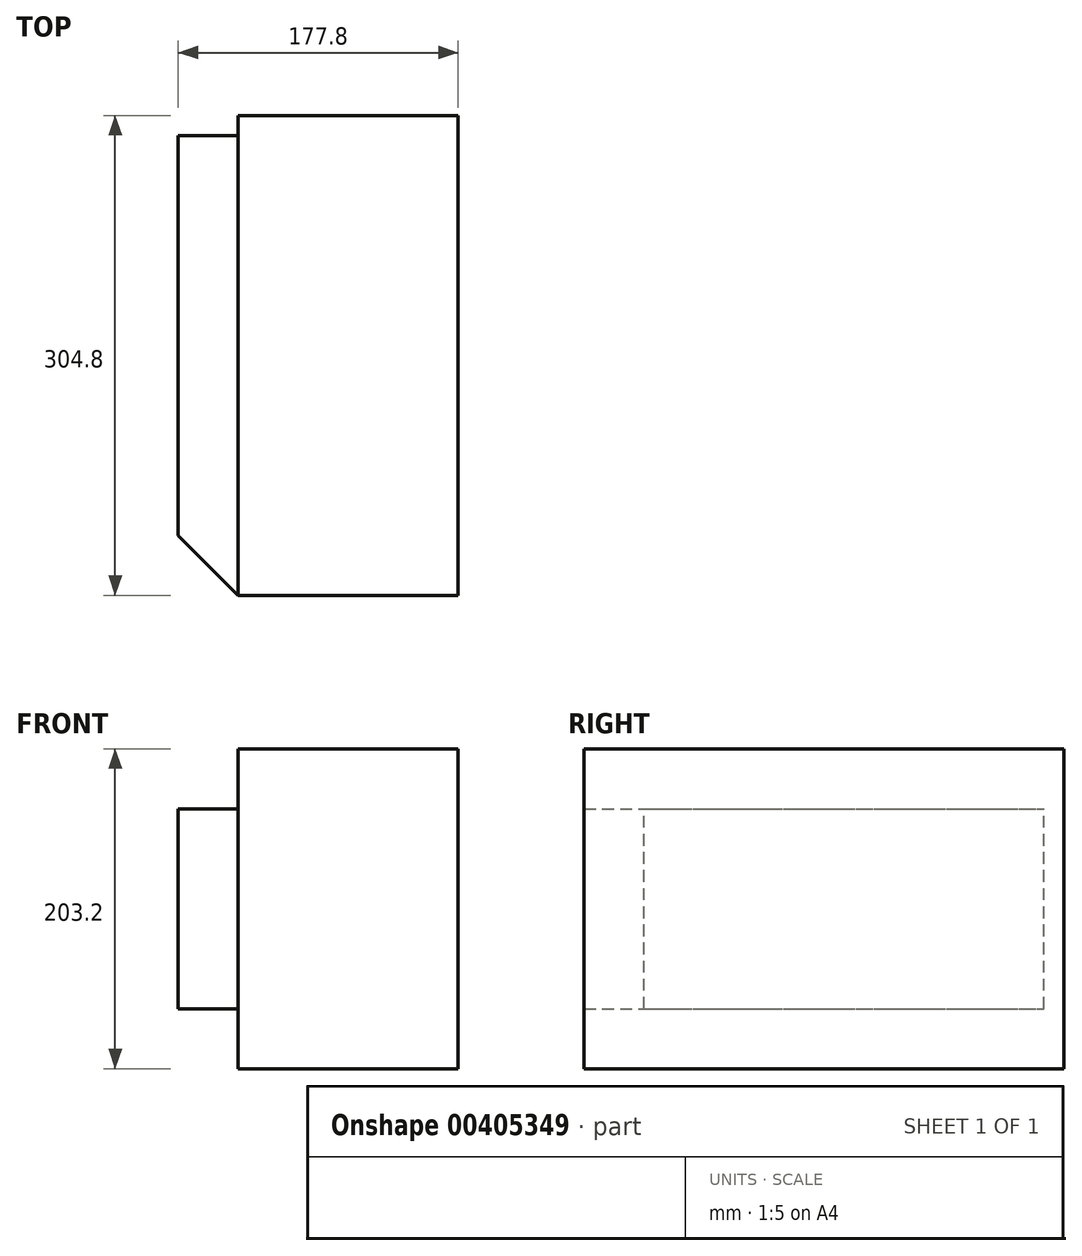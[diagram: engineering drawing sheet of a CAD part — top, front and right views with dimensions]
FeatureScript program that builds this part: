
annotation { "Feature Type Name" : "Feature", "Feature Type Description" : "" }
export const myFeature = defineFeature(function(context is Context, id is Id, definition is map)
    precondition{}
    {
        {
            var Q0;
            Q0=qCreatedBy(makeId("Front.planeOp"),FACE);
            var sketch = newSketch(context, id + "F0", { "sketchPlane" : qUnion([Q0])});
            skLineSegment(sketch, "E0.bottom", {"start": v(-126.61, 97) * mm, "end": v(51.19, 97) * mm});
            skLineSegment(sketch, "E0.top", {"start": v(-126.61, -106.2) * mm, "end": v(51.19, -106.2) * mm});
            skLineSegment(sketch, "E0.left", {"start": v(-126.61, 97) * mm, "end": v(-126.61, -106.2) * mm});
            skLineSegment(sketch, "E0.right", {"start": v(51.19, 97) * mm, "end": v(51.19, -106.2) * mm});
            skLineSegment(sketch, "E1.0", {"start": v(-88.51, 97) * mm, "end": v(-88.51, -106.2) * mm});
            skLineSegment(sketch, "E2", {"start": v(-126.61, 58.9) * mm, "end": v(-88.51, 58.9) * mm});
            skLineSegment(sketch, "E3", {"start": v(-126.61, -68.1) * mm, "end": v(-88.51, -68.1) * mm});
            skSolve(sketch);
        }
        {
            var Q0;
            {var subQ0=sQuery(id+"F0.wireOp",EDGE,"E0.right");Q0=makeQuery(id+"F0.imprint","IMPRINT",FACE,{"disambiguationData":[TD([[makeQuery(id+"F0.imprint","IMPRINT",EDGE,{"derivedFrom":subQ0}),-1.0]])]});}
            extrude(context, id + "F1", {"entities" : qUnion([Q0]), "depth" : 304.8 * mm});
        }
        {
            var Q0;
            {var subQ0=sQuery(id+"F0.wireOp",EDGE,"E2");Q0=makeQuery(id+"F0.imprint","IMPRINT",FACE,{"disambiguationData":[TD([[makeQuery(id+"F0.imprint","IMPRINT",EDGE,{"derivedFrom":subQ0}),-1.0]])]});}
            extrude(context, id + "F2", {"entities" : qUnion([Q0]), "operationType" : NewBodyOperationType.ADD, "depth" : 304.8 * mm});
        }
        {
            var Q0;
            Q0=makeQuery(id+"F2.opExtrude","SWEPT_FACE",FACE,{"disambiguationData":[OSD([sQuery(id+"F0.wireOp",EDGE,"E2")])]});
            var sketch = newSketch(context, id + "F3", { "sketchPlane" : qUnion([Q0])});
            skLineSegment(sketch, "E4", {"start": v(-126.61, -12.7) * mm, "end": v(-88.51, -12.7) * mm});
            skLineSegment(sketch, "E5", {"start": v(-88.51, -304.8) * mm, "end": v(-126.61, -266.7) * mm});
            skSolve(sketch);
        }
        {
            var Q0;
            {var subQ0=sQuery(id+"F3.wireOp",EDGE,"E4");Q0=makeQuery(id+"F3.imprint","IMPRINT",FACE,{"disambiguationData":[TD([[makeQuery(id+"F3.imprint","IMPRINT",EDGE,{"derivedFrom":subQ0}),1.0]])]});}
            var Q1;
            {var subQ0=sQuery(id+"F3.wireOp",EDGE,"E5");Q1=makeQuery(id+"F3.imprint","IMPRINT",FACE,{"disambiguationData":[TD([[makeQuery(id+"F3.imprint","IMPRINT",EDGE,{"derivedFrom":subQ0}),1.0]])]});}
            var Q2;
            Q2=sQuery(id+"F3.wireOp",EDGE,"E4");
            var Q3;
            Q3=sQuery(id+"F3.wireOp",EDGE,"E5");
            extrude(context, id + "F4", {"entities" : qUnion([Q0, Q1]), "operationType" : NewBodyOperationType.REMOVE, "surfaceEntities" : qUnion([Q2, Q3]), "endBound" : BoundingType.THROUGH_ALL, "oppositeDirection" : true, "depth" : 25.4 * mm});
        }
    });
